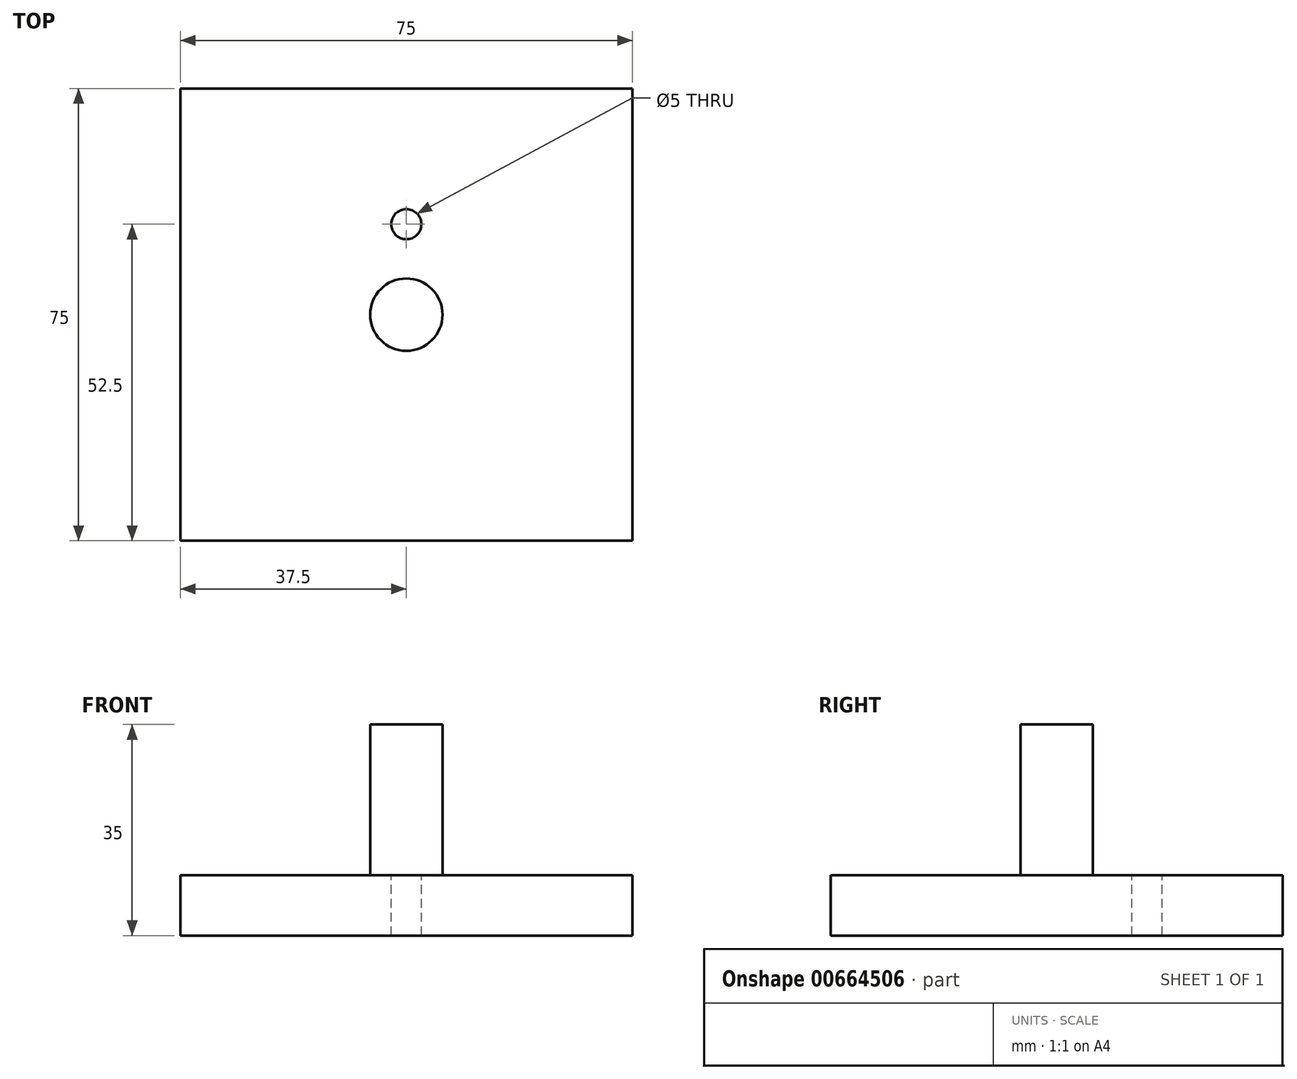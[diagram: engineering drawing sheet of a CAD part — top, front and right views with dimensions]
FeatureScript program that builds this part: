
annotation { "Feature Type Name" : "Feature", "Feature Type Description" : "" }
export const myFeature = defineFeature(function(context is Context, id is Id, definition is map)
    precondition{}
    {
        {
            var Q0;
            Q0=qCreatedBy(makeId("Top.planeOp"),FACE);
            var sketch = newSketch(context, id + "F0", { "sketchPlane" : qUnion([Q0])});
            skLineSegment(sketch, "E0.bottom", {"start": v(37.5, -37.5) * mm, "end": v(-37.5, -37.5) * mm});
            skLineSegment(sketch, "E0.top", {"start": v(37.5, 37.5) * mm, "end": v(-37.5, 37.5) * mm});
            skLineSegment(sketch, "E0.left", {"start": v(37.5, -37.5) * mm, "end": v(37.5, 37.5) * mm});
            skLineSegment(sketch, "E0.right", {"start": v(-37.5, -37.5) * mm, "end": v(-37.5, 37.5) * mm});
            skPoint(sketch, "E0.middle", {"position": v(0, 0) * mm});
            skSolve(sketch);
        }
        {
            var Q0;
            Q0 = qSketchRegion(id + "F0", true);
            extrude(context, id + "F1", {"entities" : qUnion([Q0]), "depth" : 10 * mm, "offsetDistance" : 25 * mm});
        }
        {
            var Q0;
            Q0=makeQuery(id+"F1.opExtrude","CAP_FACE",FACE,{"disambiguationData":[OSD([sQuery(id+"F0.wireOp",EDGE,"E0.bottom"),sQuery(id+"F0.wireOp",EDGE,"E0.top"),sQuery(id+"F0.wireOp",EDGE,"E0.left"),sQuery(id+"F0.wireOp",EDGE,"E0.right")])],"isStart":false});
            var sketch = newSketch(context, id + "F2", { "sketchPlane" : qUnion([Q0])});
            skCircle(sketch, "E1", {"center": v(0, 0) * mm, "radius": 6 * mm});
            skCircle(sketch, "E2", {"center": v(0, 0) * mm, "radius": 21.5 * mm});
            skLineSegment(sketch, "E3", {"start": v(0, 0) * mm, "end": v(0, 15) * mm});
            skCircle(sketch, "E4", {"center": v(0, 15) * mm, "radius": 2.5 * mm});
            skSolve(sketch);
        }
        {
            var Q0;
            Q0=makeQuery(id+"F2.imprint","IMPRINT",FACE,{"disambiguationData":[TD([[makeQuery(id+"F2.imprint","IMPRINT",EDGE,{"derivedFrom":sQuery(id+"F2.wireOp",EDGE,"E1")}),1.0]])]});
            extrude(context, id + "F3", {"entities" : qUnion([Q0]), "operationType" : NewBodyOperationType.ADD, "depth" : 25 * mm, "offsetDistance" : 25 * mm});
        }
        {
            var Q0;
            Q0=makeQuery(id+"F2.imprint","IMPRINT",FACE,{"disambiguationData":[TD([[makeQuery(id+"F2.imprint","IMPRINT",EDGE,{"derivedFrom":sQuery(id+"F2.wireOp",EDGE,"E4")}),1.0]])]});
            extrude(context, id + "F4", {"entities" : qUnion([Q0]), "operationType" : NewBodyOperationType.REMOVE, "oppositeDirection" : true, "depth" : 10 * mm, "offsetDistance" : 25 * mm});
        }
    });
